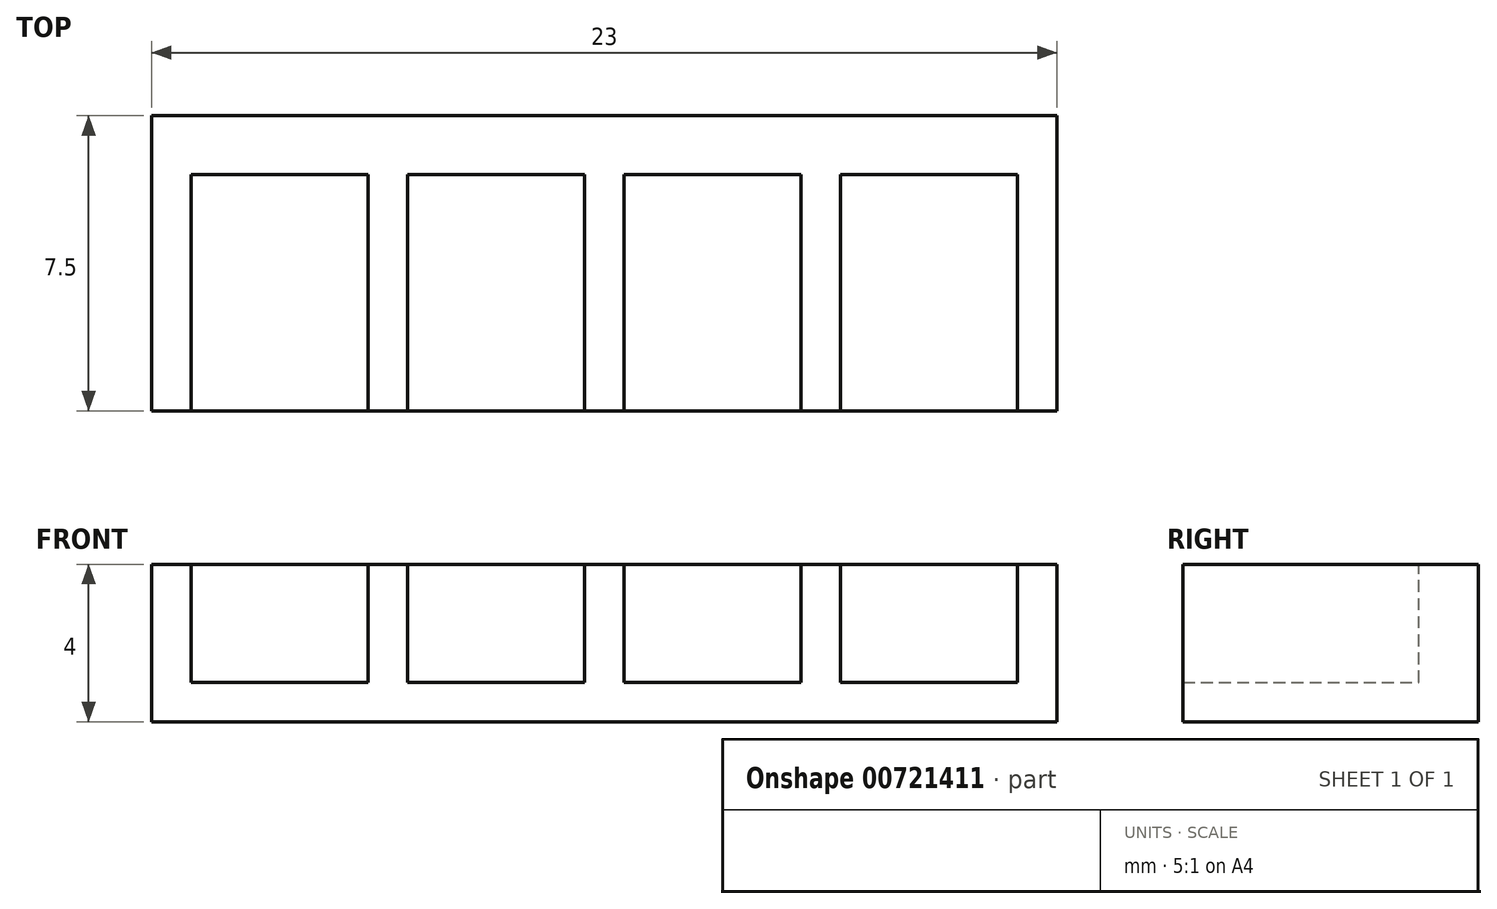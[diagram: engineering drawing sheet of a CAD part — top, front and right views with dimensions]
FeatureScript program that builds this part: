
annotation { "Feature Type Name" : "Feature", "Feature Type Description" : "" }
export const myFeature = defineFeature(function(context is Context, id is Id, definition is map)
    precondition{}
    {
        {
            var Q0;
            Q0=qCreatedBy(makeId("Top.planeOp"),FACE);
            var sketch = newSketch(context, id + "F0", { "sketchPlane" : qUnion([Q0])});
            skLineSegment(sketch, "E0.bottom", {"start": v(0, 0) * mm, "end": v(23, 0) * mm});
            skLineSegment(sketch, "E0.top", {"start": v(0, 7.5) * mm, "end": v(23, 7.5) * mm});
            skLineSegment(sketch, "E0.left", {"start": v(0, 0) * mm, "end": v(0, 7.5) * mm});
            skLineSegment(sketch, "E0.right", {"start": v(23, 0) * mm, "end": v(23, 7.5) * mm});
            skSolve(sketch);
        }
        {
            var Q0;
            Q0=makeQuery(id+"F0.imprint","IMPRINT",FACE,{"disambiguationData":[TD([[makeQuery(id+"F0.imprint","IMPRINT",EDGE,{"derivedFrom":sQuery(id+"F0.wireOp",EDGE,"E0.bottom")}),1.0]])]});
            extrude(context, id + "F1", {"entities" : qUnion([Q0]), "depth" : 4 * mm, "offsetDistance" : 25.4 * mm});
        }
        {
            var Q0;
            Q0=makeQuery(id+"F1.opExtrude","CAP_FACE",FACE,{"disambiguationData":[OSD([sQuery(id+"F0.wireOp",EDGE,"E0.bottom"),sQuery(id+"F0.wireOp",EDGE,"E0.top"),sQuery(id+"F0.wireOp",EDGE,"E0.left"),sQuery(id+"F0.wireOp",EDGE,"E0.right")])],"isStart":false});
            var sketch = newSketch(context, id + "F2", { "sketchPlane" : qUnion([Q0])});
            skLineSegment(sketch, "E1.bottom", {"start": v(1, 0) * mm, "end": v(5.5, 0) * mm});
            skLineSegment(sketch, "E1.top", {"start": v(1, 6) * mm, "end": v(5.5, 6) * mm});
            skLineSegment(sketch, "E1.left", {"start": v(1, 0) * mm, "end": v(1, 6) * mm});
            skLineSegment(sketch, "E1.right", {"start": v(5.5, 0) * mm, "end": v(5.5, 6) * mm});
            skLineSegment(sketch, "E2.bottom", {"start": v(6.5, 0) * mm, "end": v(11, 0) * mm});
            skLineSegment(sketch, "E2.top", {"start": v(6.5, 6) * mm, "end": v(11, 6) * mm});
            skLineSegment(sketch, "E2.left", {"start": v(6.5, 0) * mm, "end": v(6.5, 6) * mm});
            skLineSegment(sketch, "E2.right", {"start": v(11, 0) * mm, "end": v(11, 6) * mm});
            skLineSegment(sketch, "E3.bottom", {"start": v(12, 0) * mm, "end": v(16.5, 0) * mm});
            skLineSegment(sketch, "E3.top", {"start": v(12, 6) * mm, "end": v(16.5, 6) * mm});
            skLineSegment(sketch, "E3.left", {"start": v(12, 0) * mm, "end": v(12, 6) * mm});
            skLineSegment(sketch, "E3.right", {"start": v(16.5, 0) * mm, "end": v(16.5, 6) * mm});
            skLineSegment(sketch, "E4.bottom", {"start": v(17.5, 0) * mm, "end": v(22, 0) * mm});
            skLineSegment(sketch, "E4.top", {"start": v(17.5, 6) * mm, "end": v(22, 6) * mm});
            skLineSegment(sketch, "E4.left", {"start": v(17.5, 0) * mm, "end": v(17.5, 6) * mm});
            skLineSegment(sketch, "E4.right", {"start": v(22, 0) * mm, "end": v(22, 6) * mm});
            skSolve(sketch);
        }
        {
            var Q0;
            Q0 = qSketchRegion(id + "F2", true);
            extrude(context, id + "F3", {"entities" : qUnion([Q0]), "operationType" : NewBodyOperationType.REMOVE, "oppositeDirection" : true, "depth" : 3 * mm, "offsetDistance" : 25.4 * mm});
        }
    });
